# Revit family: RN 90078 Optifitt-Serra-Nippel doppio
name_source: partatom
category: Rohrformteile
units: mm (PartAtom-declared; Revit-internal decimal feet)

## family parameters
Arbeitsebenenbasiert = Nein
Beim Laden mit Abzugskörper schneiden = Nein
Bemaßung runder Anschluss = Durchmesser verwenden
Gemeinsam genutzt = Nein
Immer vertikal = Ja
Teiletyp = Nicht definiert

## types (6) — shared parameters
1.010.00.2 Blattnummer der Richtlinie = 29
1.010.00.3 Ausgabedatum (Monat) der Richtlinie = 201308
1.010.00.4 Herstellername = R. Nussbaum AG
1.010.00.5 Revisionsdatum der Datei = 20190521
1.010.00.6 Webadresse des Herstellers = http://www.nussbaum.ch
1.100.00.4 Produktbezeichnung = Versorgung
1.110.00.2 Index = 3
1.110.00.4 Produktbezeichnung = Optifitt-Serra
1.960/3L.00.8 Link (URL) = https://www.nussbaum.ch
29.700.00.4 Produktname = Optifitt-Serra-Doppelnippel
29.700.00.5 Produktkennung = 2
29.700.00.6 Querschnittsform = 1
29.700.00.7 Nennweitensystem = DN
29.700.00.8 Nenndrucksystem = PN
29.710.02.4 Nenndruck = 16
29.710.02.5 max. zul. Überdruck [hPa] = 1600
29.710.02.7 max. zul. Dauer-Betriebsdruck [hPa] = 1600
29.710.02.9 max. zul. Dauer-Betriebstemperatur [°C] = 90
Connector Visibility = Nein
EnclosingSpace Visibility = Nein
Hersteller = R. Nussbaum AG
R. Nussbaum AG 90078.04 de Visibility = Nein
URL = https://www.nussbaum.ch

## per-type parameters (varying)
| type | 1.800.00.3 TGA-Nummer | 1.800.00.4 Kommentarfeld | 1.810.00.3 Hersteller-Bestellnummer | 1.810.00.4 DATANORM-Nummer | 1.810.00.5 StLB-Nummer | 1.810.00.6 GTIN-Nummer | 29.710.02.10 Formstück-Gewicht [kg] | 29.710.02.3 Benennung | CONNECTOR0_DIAMETER_dX_0r | CONNECTOR0_dX_01 | CONNECTOR0_ref_dX | CONNECTOR1_DIAMETER_dX_0r | CONNECTOR1_dX_00 | CONNECTOR1_dX_01 | CONNECTOR1_ref_dX | Modell | R. Nussbaum AG 90078.05 de Visibility | R. Nussbaum AG 90078.06 de Visibility | R. Nussbaum AG 90078.07 de Visibility | R. Nussbaum AG 90078.08 de Visibility | R. Nussbaum AG 90078.09 de Visibility | R. Nussbaum AG 90078.10 de Visibility | Typenkommentare |
| DN=65 | 01900300000000000000000000000000000000000000000015000000000000000021 | 90078.10, Optifitt-Serra-Doppelnippel, DN=65, L=70, R=2½ | 90078.1 | 90078.1 | 214.318 | 7612945680327 | 0.69 | Optifitt-Serra-Doppelnippel, DN=65, L=70, R=2½ | 65 mm | 27 mm | 27 mm | 65 mm | 43 mm | 70 mm | 70 mm | 90078.1 | Nein | Nein | Nein | Nein | Nein | Ja | Optifitt-Serra-Nippel doppio  DN=65 |
| DN=50 | 01900300000000000000000000000000000000000000000015000000000000000014 | 90078.09, Optifitt-Serra-Doppelnippel, DN=50, L=62, R=2 | 90078.09 | 90078.09 | 214.317 | 7612945680310 | 0.419 | Optifitt-Serra-Doppelnippel, DN=50, L=62, R=2 | 50 mm  [stored 0.164042 ft] | 24 mm | 24 mm | 50 mm  [stored 0.164042 ft] | 38 mm | 62 mm | 62 mm | 90078.09 | Nein | Nein | Nein | Nein | Ja | Nein | Optifitt-Serra-Nippel doppio  DN=50 |
| DN=40 | 01900300000000000000000000000000000000000000000015000000000000000013 | 90078.08, Optifitt-Serra-Doppelnippel, DN=40, L=54, R=1½ | 90078.08 | 90078.08 | 214.316 | 7612945680303 | 0.265 | Optifitt-Serra-Doppelnippel, DN=40, L=54, R=1½ | 40 mm  [stored 0.131234 ft] | 19 mm | 19 mm | 40 mm  [stored 0.131234 ft] | 35 mm  [stored 0.114829 ft] | 54 mm | 54 mm | 90078.08 | Nein | Nein | Nein | Ja | Nein | Nein | Optifitt-Serra-Nippel doppio  DN=40 |
| DN=32 | 01900300000000000000000000000000000000000000000015000000000000000012 | 90078.07, Optifitt-Serra-Doppelnippel, DN=32, L=53, R=1¼ | 90078.07 | 90078.07 | 214.315 | 7612945680297 | 0.23 | Optifitt-Serra-Doppelnippel, DN=32, L=53, R=1¼ | 32 mm | 19 mm | 19 mm | 32 mm | 34 mm  [stored 0.111549 ft] | 53 mm | 53 mm | 90078.07 | Nein | Nein | Ja | Nein | Nein | Nein | Optifitt-Serra-Nippel doppio  DN=32 |
| DN=25 | 01900300000000000000000000000000000000000000000015000000000000000011 | 90078.06, Optifitt-Serra-Doppelnippel, DN=25, L=46, R=1 | 90078.06 | 90078.06 | 214.314 | 7612945680280 | 0.114 | Optifitt-Serra-Doppelnippel, DN=25, L=46, R=1 | 25 mm  [stored 0.082021 ft] | 17 mm | 17 mm | 25 mm  [stored 0.082021 ft] | 29 mm | 46 mm | 46 mm | 90078.06 | Nein | Ja | Nein | Nein | Nein | Nein | Optifitt-Serra-Nippel doppio  DN=25 |
| DN=20 | 01900300000000000000000000000000000000000000000015000000000000000010 | 90078.05, Optifitt-Serra-Doppelnippel, DN=20, L=40, R=¾ | 90078.05 | 90078.05 | 214.313 | 7612945680273 | 0.083 | Optifitt-Serra-Doppelnippel, DN=20, L=40, R=¾ | 20 mm  [stored 0.0656168 ft] | 15 mm | 15 mm | 20 mm  [stored 0.0656168 ft] | 25 mm  [stored 0.082021 ft] | 40 mm  [stored 0.131234 ft] | 40 mm  [stored 0.131234 ft] | 90078.05 | Ja | Nein | Nein | Nein | Nein | Nein | Optifitt-Serra-Nippel doppio  DN=20 |

note: [stored X ft] marks values corroborated as IEEE doubles in the binary element streams (Revit-internal decimal feet)

## geometry (parser evidence)
native form markers: Sweep x2
no freeform markers — native parametric forms only
